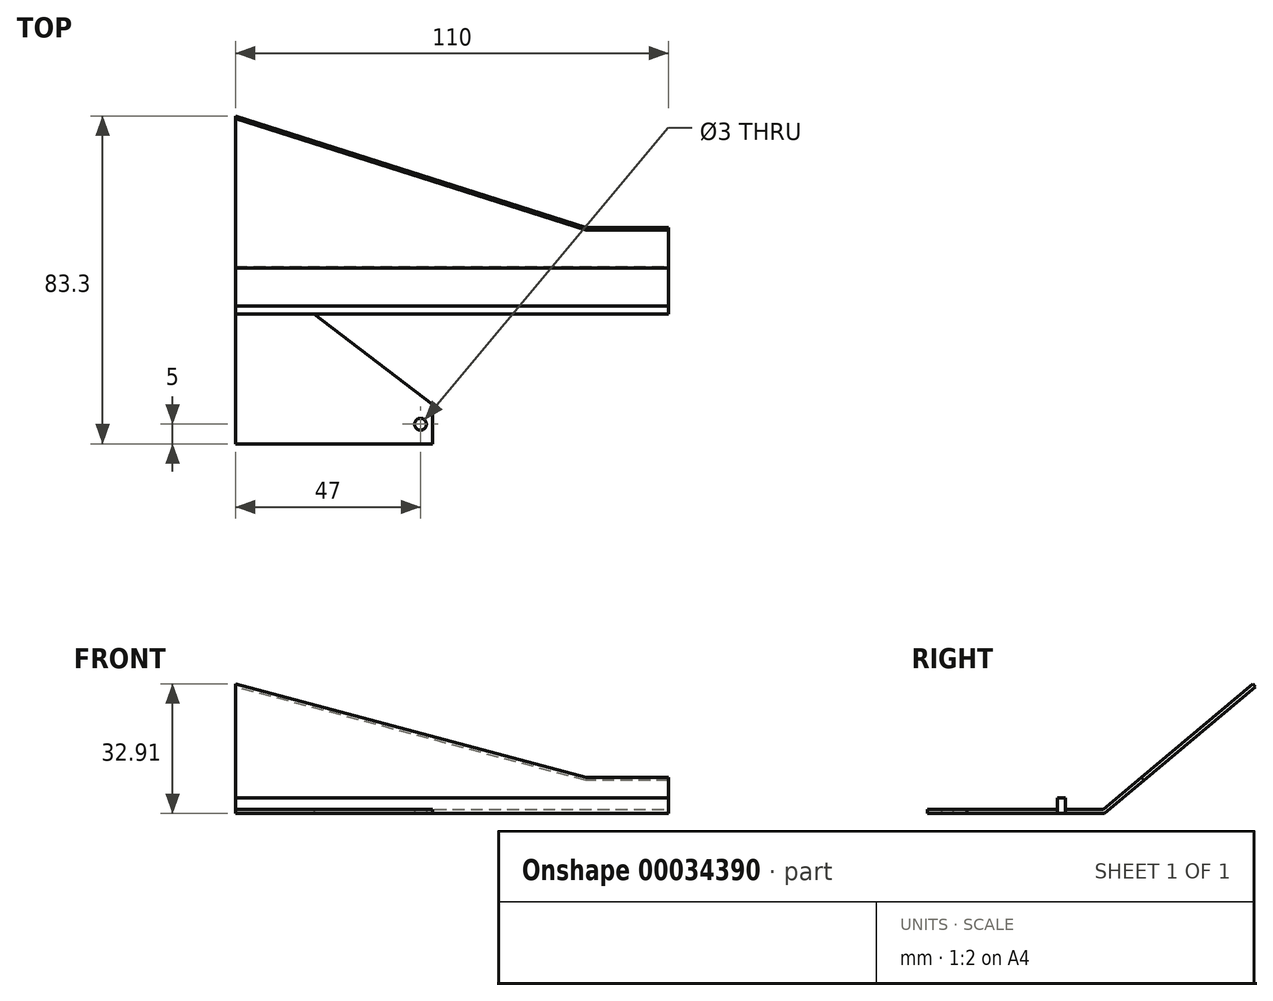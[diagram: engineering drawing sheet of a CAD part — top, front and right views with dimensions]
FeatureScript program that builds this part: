
annotation { "Feature Type Name" : "Feature", "Feature Type Description" : "" }
export const myFeature = defineFeature(function(context is Context, id is Id, definition is map)
    precondition{}
    {
        {
            var Q0;
            Q0=qCreatedBy(makeId("Top.planeOp"),FACE);
            var sketch = newSketch(context, id + "F0", { "sketchPlane" : qUnion([Q0])});
            skLineSegment(sketch, "E0", {"start": v(0, 0) * mm, "end": v(50, 0) * mm});
            skLineSegment(sketch, "E1", {"start": v(50, 0) * mm, "end": v(50, 10) * mm});
            skLineSegment(sketch, "E2", {"start": v(50, 10) * mm, "end": v(20, 33) * mm});
            skLineSegment(sketch, "E3", {"start": v(20, 33) * mm, "end": v(0, 33) * mm});
            skLineSegment(sketch, "E4", {"start": v(0, 33) * mm, "end": v(0, 0) * mm});
            skLineSegment(sketch, "E5.bottom", {"start": v(0, 33) * mm, "end": v(110, 33) * mm});
            skLineSegment(sketch, "E5.top", {"start": v(0, 35) * mm, "end": v(110, 35) * mm});
            skLineSegment(sketch, "E5.left", {"start": v(0, 33) * mm, "end": v(0, 35) * mm});
            skLineSegment(sketch, "E5.right", {"start": v(110, 33) * mm, "end": v(110, 35) * mm});
            skLineSegment(sketch, "E6.top", {"start": v(0, 45) * mm, "end": v(110, 45) * mm});
            skLineSegment(sketch, "E6.left", {"start": v(0, 33) * mm, "end": v(0, 45) * mm});
            skLineSegment(sketch, "E6.right", {"start": v(110, 33) * mm, "end": v(110, 45) * mm});
            skCircle(sketch, "E7", {"center": v(47, 5) * mm, "radius": 3 * mm});
            skCircle(sketch, "E8", {"center": v(47, 5) * mm, "radius": 1.5 * mm});
            skSolve(sketch);
        }
        {
            var Q0;
            {var subQ2=sQuery(id+"F0.wireOp",EDGE,"E5.top");Q0=makeQuery(id+"F0.imprint","IMPRINT",FACE,{"disambiguationData":[TD([[makeQuery(id+"F0.imprint","IMPRINT",EDGE,{"derivedFrom":subQ2}),1.0]])]});}
            var Q1;
            {var subQ6=sQuery(id+"F0.wireOp",EDGE,"E0");Q1=makeQuery(id+"F0.imprint","IMPRINT",FACE,{"disambiguationData":[TD([[makeQuery(id+"F0.imprint","IMPRINT",EDGE,{"derivedFrom":subQ6}),1.0]])]});}
            var Q2;
            Q2=makeQuery(id+"F0.imprint","IMPRINT",FACE,{"disambiguationData":[TD([[makeQuery(id+"F0.imprint","IMPRINT",EDGE,{"derivedFrom":sQuery(id+"F0.wireOp",EDGE,"E7")}),1.0]])]});
            extrude(context, id + "F1", {"entities" : qUnion([Q0, Q1, Q2]), "depth" : 1 * mm});
        }
        {
            var Q0;
            {var subQ3=sQuery(id+"F0.wireOp",EDGE,"E5.top");Q0=makeQuery(id+"F0.imprint","IMPRINT",FACE,{"disambiguationData":[TD([[makeQuery(id+"F0.imprint","IMPRINT",EDGE,{"derivedFrom":subQ3}),-1.0]])]});}
            extrude(context, id + "F2", {"entities" : qUnion([Q0]), "depth" : 4 * mm});
        }
        {
            var Q0;
            Q0=sQuery(id+"F0.wireOp",EDGE,"E6.top");
            cPlane(context, id + "F3", {"entities" : qUnion([Q0]), "cplaneType" : CPlaneType.LINE_ANGLE, "offset" : 150 * mm, "angle" : 130 * degree, "width" : 150 * mm, "height" : 150 * mm});
        }
        {
            var Q0;
            Q0=qCreatedBy(id+"F3.planeOp",FACE);
            var sketch = newSketch(context, id + "F4", { "sketchPlane" : qUnion([Q0])});
            skLineSegment(sketch, "E9", {"start": v(0, 34.47) * mm, "end": v(110, 34.47) * mm});
            skLineSegment(sketch, "E10", {"start": v(110, 34.47) * mm, "end": v(110, 47.47) * mm});
            skLineSegment(sketch, "E11", {"start": v(110, 47.47) * mm, "end": v(89, 47.47) * mm});
            skLineSegment(sketch, "E12", {"start": v(89, 47.47) * mm, "end": v(0, 84.47) * mm});
            skLineSegment(sketch, "E13", {"start": v(0, 84.47) * mm, "end": v(0, 34.47) * mm});
            skSolve(sketch);
        }
        {
            var Q0;
            Q0=makeQuery(id+"F4.imprint","IMPRINT",FACE,{"disambiguationData":[TD([[makeQuery(id+"F4.imprint","IMPRINT",EDGE,{"derivedFrom":sQuery(id+"F4.wireOp",EDGE,"E9")}),1.0]])]});
            extrude(context, id + "F5", {"entities" : qUnion([Q0]), "operationType" : NewBodyOperationType.ADD, "depth" : 1 * mm});
        }
    });
